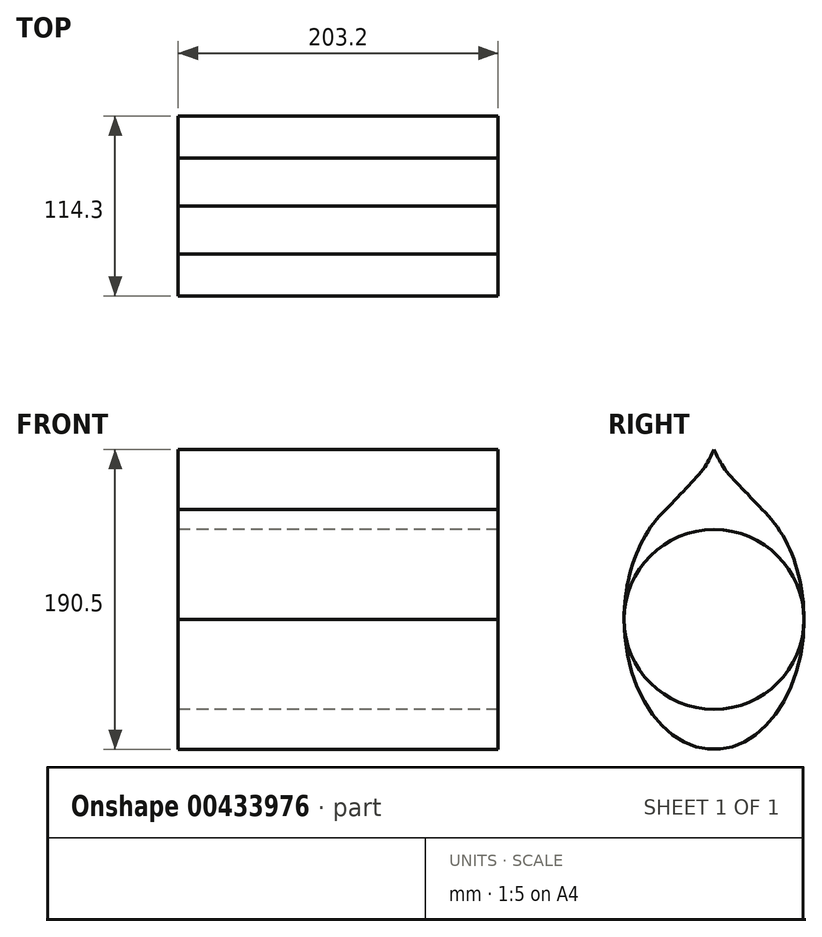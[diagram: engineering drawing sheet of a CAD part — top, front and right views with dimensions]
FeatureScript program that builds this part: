
annotation { "Feature Type Name" : "Feature", "Feature Type Description" : "" }
export const myFeature = defineFeature(function(context is Context, id is Id, definition is map)
    precondition{}
    {
        {
            var Q0;
            Q0=qCreatedBy(makeId("Right.planeOp"),FACE);
            var sketch = newSketch(context, id + "F0", { "sketchPlane" : qUnion([Q0])});
            skCircle(sketch, "E0", {"center": v(0, 0) * mm, "radius": 57.15 * mm});
            skEllipticalArc(sketch, "E1", {});
            skLineSegment(sketch, "E2", {"start": v(0, 82.55) * mm, "end": v(0, 107.95) * mm, "construction": true});
            skLineSegment(sketch, "E3", {"start": v(0, 82.55) * mm, "end": v(0, 57.15) * mm, "construction": true});
            skPoint(sketch, "E4.0.internal.snap0", {"position": v(0, 69.85) * mm});
            skPoint(sketch, "E4.1.internal.snap0", {"position": v(0, 95.25) * mm});
            skFitSpline(sketch, "E4", {"points": [v(30.46, 69.85) * mm, v(7.1, 95.25) * mm, v(0, 107.95) * mm], "startDerivative": vector(-40.1, 45.42) * mm, "endDerivative": vector(-14.34, 29.73) * mm});
            skFitSpline(sketch, "E5.MirrorCS", {"points": [v(-30.46, 69.85) * mm, v(-7.1, 95.25) * mm, v(0, 107.95) * mm], "startDerivative": vector(40.1, 45.42) * mm, "endDerivative": vector(14.34, 29.73) * mm});
            const initialGuessF0  = {"E1": [0, 0, 0, 1, 0.08255, 0.05715, 0.562069803005627, 5.721115504173959]};
            skSetInitialGuess(sketch, initialGuessF0);
            skSolve(sketch);
        }
        {
            var Q0;
            {var subQ0=sQuery(id+"F0.wireOp",EDGE,"E4");Q0=makeQuery(id+"F0.imprint","IMPRINT",FACE,{"disambiguationData":[TD([[makeQuery(id+"F0.imprint","IMPRINT",EDGE,{"derivedFrom":subQ0}),1.0]])]});}
            var Q1;
            {var subQ0=sQuery(id+"F0.wireOp",EDGE,"E1");var subQ1=sQuery(id+"F0.wireOp",EDGE,"E0");var subQ2=makeQuery(id+"F0.imprint","INTERSECT",VERTEX,{"disambiguationData":[OD(0.0)],"derivedFrom":[subQ1,subQ0]});Q1=makeQuery(id+"F0.imprint","IMPRINT",FACE,{"disambiguationData":[TD([[makeQuery(id+"F0.imprint","IMPRINT",EDGE,{"disambiguationData":[TD([[subQ2,-1.0]])],"derivedFrom":subQ1}),-1.0]])]});}
            extrude(context, id + "F1", {"entities" : qUnion([Q0, Q1]), "depth" : 203.2 * mm});
        }
    });
